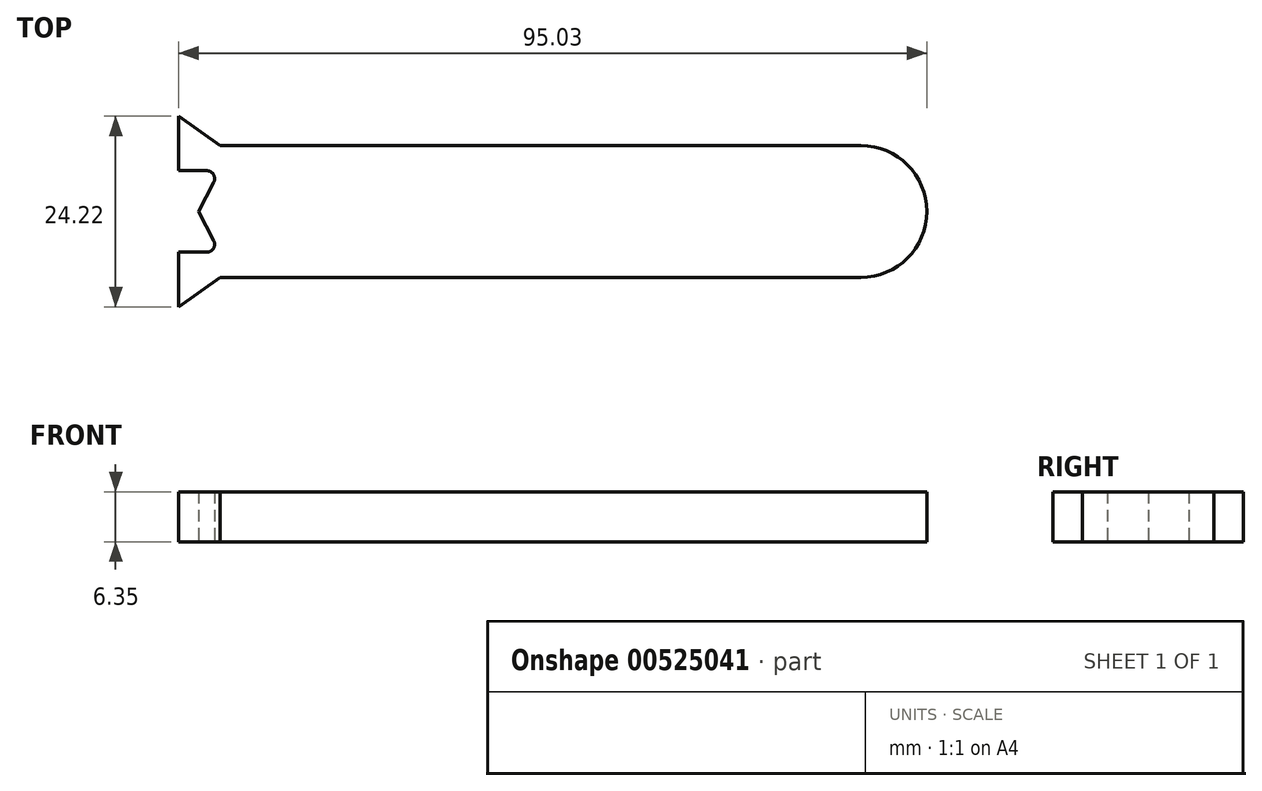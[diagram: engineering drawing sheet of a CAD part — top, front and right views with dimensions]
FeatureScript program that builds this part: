
annotation { "Feature Type Name" : "Feature", "Feature Type Description" : "" }
export const myFeature = defineFeature(function(context is Context, id is Id, definition is map)
    precondition{}
    {
        {
            var Q0;
            Q0=qCreatedBy(makeId("Top.planeOp"),FACE);
            var sketch = newSketch(context, id + "F0", { "sketchPlane" : qUnion([Q0])});
            skLineSegment(sketch, "E0.bottom", {"start": v(40.72, 8.37) * mm, "end": v(-40.72, 8.37) * mm});
            skLineSegment(sketch, "E0.top", {"start": v(40.72, -8.37) * mm, "end": v(-40.72, -8.37) * mm});
            skPoint(sketch, "E0.middle", {"position": v(0, 0) * mm});
            skArc(sketch, "E1", {"start": v(40.72, 8.37) * mm, "mid": v(49.1, 0) * mm, "end": v(40.72, -8.37) * mm});
            skLineSegment(sketch, "E2", {"start": v(-45.94, 8.37) * mm, "end": v(-45.94, 12.1) * mm});
            skLineSegment(sketch, "E3", {"start": v(-45.94, 12.1) * mm, "end": v(-40.72, 8.37) * mm});
            skLineSegment(sketch, "E4.MirrorCS", {"start": v(-45.94, -12.1) * mm, "end": v(-40.72, -8.37) * mm});
            skLineSegment(sketch, "E5.MirrorCS", {"start": v(-45.94, -8.37) * mm, "end": v(-45.94, -12.1) * mm});
            skLineSegment(sketch, "E6", {"start": v(-45.94, 8.37) * mm, "end": v(-45.94, 5.18) * mm});
            skLineSegment(sketch, "E7", {"start": v(-45.94, 5.18) * mm, "end": v(-42.4, 5.18) * mm});
            skLineSegment(sketch, "E8.MirrorCS", {"start": v(-45.94, -5.18) * mm, "end": v(-42.4, -5.18) * mm});
            skLineSegment(sketch, "E9.MirrorCS", {"start": v(-45.94, -8.37) * mm, "end": v(-45.94, -5.18) * mm});
            skLineSegment(sketch, "E10", {"start": v(-41.5, 3.7) * mm, "end": v(-43.44, 0) * mm});
            skLineSegment(sketch, "E11", {"start": v(-43.44, 0) * mm, "end": v(-41.5, -3.7) * mm});
            skPoint(sketch, "E12.visualSharp", {"position": v(-40.72, 5.18) * mm});
            skArc(sketch, "E12.filletArc", {"start": v(-41.5, 3.7) * mm, "mid": v(-41.53, 4.7) * mm, "end": v(-42.4, 5.18) * mm});
            skPoint(sketch, "E13.visualSharp", {"position": v(-40.72, -5.18) * mm});
            skArc(sketch, "E13.filletArc", {"start": v(-42.4, -5.18) * mm, "mid": v(-41.53, -4.7) * mm, "end": v(-41.5, -3.7) * mm});
            skPoint(sketch, "E14.MirrorCS.end.orphan", {"position": v(-45.94, -8.37) * mm});
            skPoint(sketch, "E14.MirrorCS.start.orphan", {"position": v(-40.72, -8.37) * mm});
            skSolve(sketch);
        }
        {
            var Q0;
            Q0 = qSketchRegion(id + "F0", true);
            extrude(context, id + "F1", {"entities" : qUnion([Q0]), "depth" : 6.35 * mm, "offsetDistance" : 25.4 * mm});
        }
    });
